# Revit family: 63002 PRESTO 504
name_source: partatom
category: Appareils sanitaires
units: mm (PartAtom-declared; Revit-internal decimal feet)

## family parameters
Cote de connecteur circulaire = Utiliser le diamètre
Couper avec des vides une fois chargée = Non
Hôte = Mur
Numéro OmniClass = 23.45.55.14
Partagée = Non
Point de calcul de pièce = Non
Titre OmniClass = Single Faucets
Toujours verticalement = Oui
Type d'élément = Normal

## types (1)
- 63002 PRESTO 504
    Description = Robinet simple temporisé pour lavabo avec rosace - eau chaude
    Durée = 15 seconds (± 5 sec.)
    Elévation par défaut = 0 mm  [stored 0 ft]
    Fabricant = LES ROBINETS PRESTO S.A.
    Famille produit = Lavabo
    Groupe produit = Temporisé
    Materiau principal = Laiton
    Materiau secondaire = Chrome
    Modèle = 63002 PRESTO 504
    Nom du fabricant = Presto
    Pays designer = France
    Pays fabricant = France
    Poids Net (Kg) = 0
    Product SKU = 63002
    Résistance thermique (30 minutes) = 75 °C
    UNSPSC Code = 301815
    URL = http://www.prestodatashare.com

note: [stored X ft] marks values corroborated as IEEE doubles in the binary element streams (Revit-internal decimal feet)

## geometry (parser evidence)
native form markers: Blend x1, Sweep x10
no freeform markers — native parametric forms only
